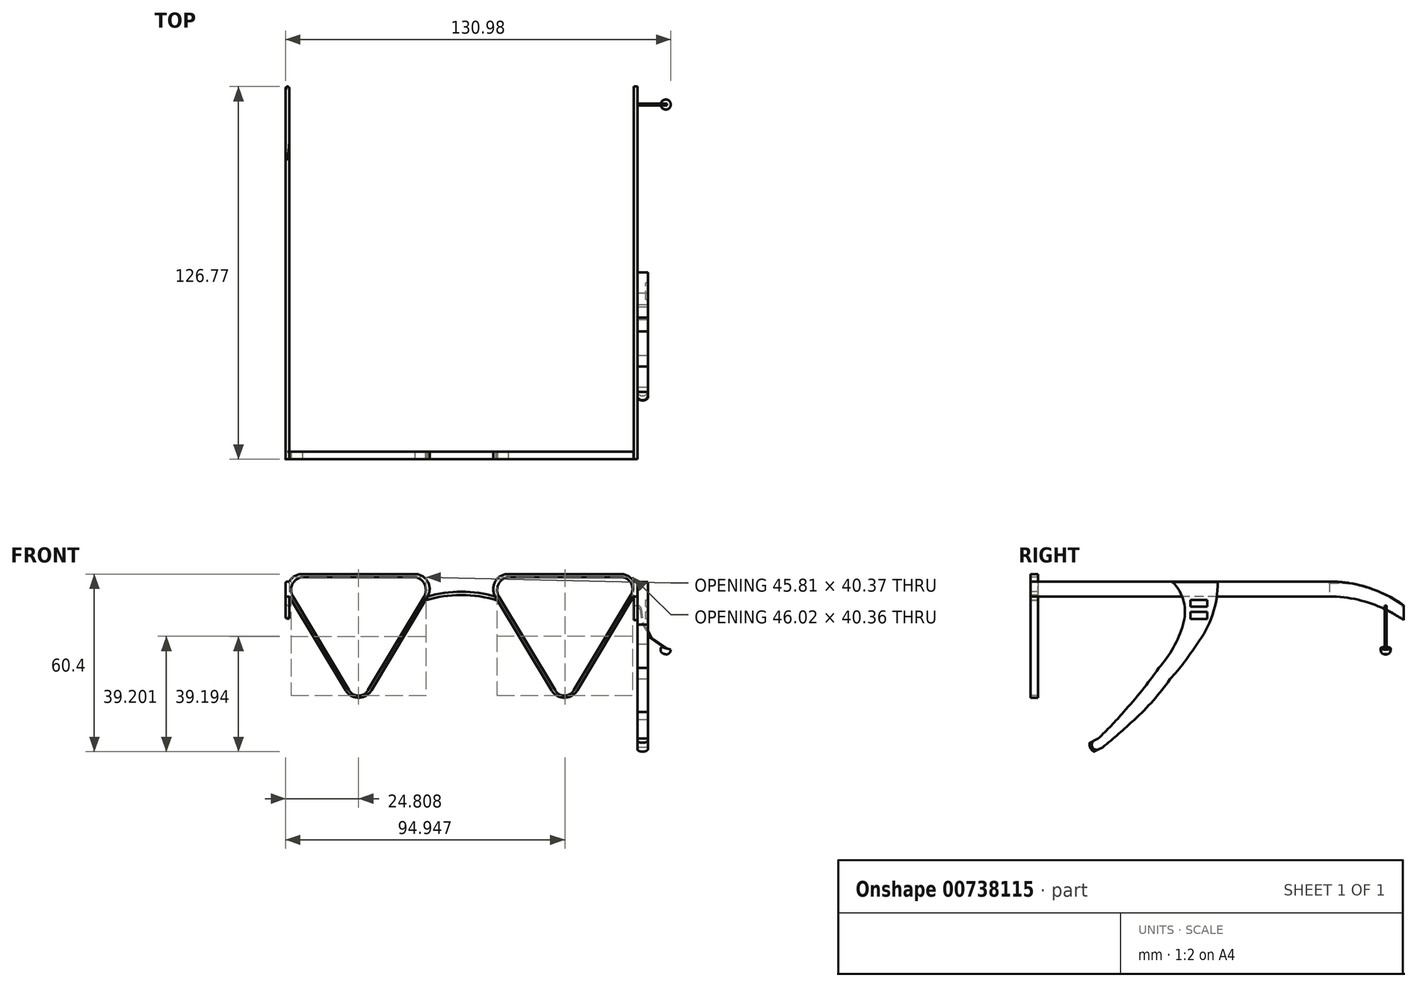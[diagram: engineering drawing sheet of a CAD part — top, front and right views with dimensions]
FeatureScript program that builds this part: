
annotation { "Feature Type Name" : "Feature", "Feature Type Description" : "" }
export const myFeature = defineFeature(function(context is Context, id is Id, definition is map)
    precondition{}
    {
        {
            var Q0;
            Q0=qCreatedBy(makeId("Front.planeOp"),FACE);
            var sketch = newSketch(context, id + "F0", { "sketchPlane" : qUnion([Q0])});
            skLineSegment(sketch, "E0", {"start": v(-99.97, 30.52) * mm, "end": v(-43.84, 30.52) * mm});
            skLineSegment(sketch, "E1", {"start": v(-71.9, -16.35) * mm, "end": v(-43.84, 30.52) * mm});
            skLineSegment(sketch, "E2", {"start": v(-99.97, 30.52) * mm, "end": v(-71.9, -16.35) * mm});
            skLineSegment(sketch, "E3.MirrorCS", {"start": v(-1.92, -16.35) * mm, "end": v(-29.99, 30.52) * mm});
            skLineSegment(sketch, "E4.MirrorCS", {"start": v(26.15, 30.52) * mm, "end": v(-29.99, 30.52) * mm});
            skLineSegment(sketch, "E5.MirrorCS", {"start": v(26.15, 30.52) * mm, "end": v(-1.92, -16.35) * mm});
            skSolve(sketch);
        }
        {
            var Q0;
            Q0=makeQuery(id+"F0.imprint","IMPRINT",FACE,{"disambiguationData":[TD([[makeQuery(id+"F0.imprint","IMPRINT",EDGE,{"derivedFrom":sQuery(id+"F0.wireOp",EDGE,"E0")}),-1.0]])]});
            var Q1;
            Q1=makeQuery(id+"F0.imprint","IMPRINT",FACE,{"disambiguationData":[TD([[makeQuery(id+"F0.imprint","IMPRINT",EDGE,{"derivedFrom":sQuery(id+"F0.wireOp",EDGE,"E3.MirrorCS")}),-1.0]])]});
            extrude(context, id + "F1", {"entities" : qUnion([Q0, Q1]), "depth" : 2.54 * mm, "offsetDistance" : 25.4 * mm});
        }
        {
            var Q0;
            Q0=makeQuery(id+"F1.opExtrude","SWEPT_EDGE",EDGE,{"disambiguationData":[OSD([sQuery(id+"F0.wireOp",EDGE,"E0"),sQuery(id+"F0.wireOp",EDGE,"E2")])]});
            var Q1;
            Q1=makeQuery(id+"F1.opExtrude","SWEPT_EDGE",EDGE,{"disambiguationData":[OSD([sQuery(id+"F0.wireOp",EDGE,"E3.MirrorCS"),sQuery(id+"F0.wireOp",EDGE,"E4.MirrorCS")])]});
            var Q2;
            Q2=makeQuery(id+"F1.opExtrude","SWEPT_EDGE",EDGE,{"disambiguationData":[OSD([sQuery(id+"F0.wireOp",EDGE,"E0"),sQuery(id+"F0.wireOp",EDGE,"E1")])]});
            var Q3;
            Q3=makeQuery(id+"F1.opExtrude","SWEPT_EDGE",EDGE,{"disambiguationData":[OSD([sQuery(id+"F0.wireOp",EDGE,"E4.MirrorCS"),sQuery(id+"F0.wireOp",EDGE,"E5.MirrorCS")])]});
            var Q4;
            Q4=makeQuery(id+"F1.opExtrude","SWEPT_EDGE",EDGE,{"disambiguationData":[OSD([sQuery(id+"F0.wireOp",EDGE,"E1"),sQuery(id+"F0.wireOp",EDGE,"E2")])]});
            var Q5;
            Q5=makeQuery(id+"F1.opExtrude","SWEPT_EDGE",EDGE,{"disambiguationData":[OSD([sQuery(id+"F0.wireOp",EDGE,"E3.MirrorCS"),sQuery(id+"F0.wireOp",EDGE,"E5.MirrorCS")])]});
            fillet(context, id + "F2", {"entities" : qUnion([Q0, Q1, Q2, Q3, Q4, Q5]), "radius" : 5.08 * mm, "tangentPropagation" : true, "allowEdgeOverflow" : false});
        }
        {
            var Q0;
            Q0=makeQuery(id+"F1.opExtrude","CAP_FACE",FACE,{"disambiguationData":[OSD([sQuery(id+"F0.wireOp",EDGE,"E0"),sQuery(id+"F0.wireOp",EDGE,"E1"),sQuery(id+"F0.wireOp",EDGE,"E2")])],"isStart":false});
            var sketch = newSketch(context, id + "F3", { "sketchPlane" : qUnion([Q0])});
            skArc(sketch, "E6", {"start": v(-25.37, 22.83) * mm, "mid": v(-36.9, 24.47) * mm, "end": v(-48.44, 22.83) * mm});
            skArc(sketch, "E7", {"start": v(-24.64, 21.5) * mm, "mid": v(-36.93, 23.39) * mm, "end": v(-49.22, 21.52) * mm});
            skLineSegment(sketch, "E8", {"start": v(-48.44, 22.83) * mm, "end": v(-49.22, 21.52) * mm});
            skLineSegment(sketch, "E9", {"start": v(-25.37, 22.83) * mm, "end": v(-24.64, 21.5) * mm});
            skSolve(sketch);
        }
        {
            var Q0;
            Q0=makeQuery(id+"F3.imprint","IMPRINT",FACE,{"disambiguationData":[TD([[makeQuery(id+"F3.imprint","IMPRINT",EDGE,{"derivedFrom":sQuery(id+"F3.wireOp",EDGE,"E6")}),1.0]])]});
            extrude(context, id + "F4", {"entities" : qUnion([Q0]), "oppositeDirection" : true, "depth" : 2.54 * mm, "offsetDistance" : 25.4 * mm});
        }
        {
            var Q0;
            Q0=makeQuery(id+"F1.opExtrude","CAP_FACE",FACE,{"disambiguationData":[OSD([sQuery(id+"F0.wireOp",EDGE,"E0"),sQuery(id+"F0.wireOp",EDGE,"E1"),sQuery(id+"F0.wireOp",EDGE,"E2")])],"isStart":false});
            var sketch = newSketch(context, id + "F5", { "sketchPlane" : qUnion([Q0])});
            skLineSegment(sketch, "E10", {"start": v(-94.18, 22.83) * mm, "end": v(-75.08, -9.07) * mm});
            skLineSegment(sketch, "E11", {"start": v(-91, 29.5) * mm, "end": v(-52.8, 29.5) * mm});
            skLineSegment(sketch, "E12", {"start": v(-49.62, 22.83) * mm, "end": v(-68.73, -9.07) * mm});
            skArc(sketch, "E13", {"start": v(-49.62, 22.83) * mm, "mid": v(-49.42, 27.01) * mm, "end": v(-52.8, 29.5) * mm});
            skArc(sketch, "E14", {"start": v(-91, 29.5) * mm, "mid": v(-94.38, 27.01) * mm, "end": v(-94.18, 22.83) * mm});
            skArc(sketch, "E15", {"start": v(-75.08, -9.07) * mm, "mid": v(-71.9, -10.87) * mm, "end": v(-68.73, -9.07) * mm});
            skSolve(sketch);
        }
        {
            var Q0;
            Q0=makeQuery(id+"F1.opExtrude","CAP_FACE",FACE,{"disambiguationData":[OSD([sQuery(id+"F0.wireOp",EDGE,"E3.MirrorCS"),sQuery(id+"F0.wireOp",EDGE,"E4.MirrorCS"),sQuery(id+"F0.wireOp",EDGE,"E5.MirrorCS")])],"isStart":false});
            var sketch = newSketch(context, id + "F6", { "sketchPlane" : qUnion([Q0])});
            skLineSegment(sketch, "E16", {"start": v(-24.15, 22.83) * mm, "end": v(-5.05, -9.07) * mm});
            skLineSegment(sketch, "E17", {"start": v(-21.02, 29.5) * mm, "end": v(17.19, 29.5) * mm});
            skLineSegment(sketch, "E18", {"start": v(20.67, 23.35) * mm, "end": v(1.26, -9.07) * mm});
            skArc(sketch, "E19", {"start": v(-21.02, 29.5) * mm, "mid": v(-24.36, 27) * mm, "end": v(-24.15, 22.83) * mm});
            skArc(sketch, "E20", {"start": v(20.67, 23.35) * mm, "mid": v(20.72, 27.44) * mm, "end": v(17.19, 29.5) * mm});
            skArc(sketch, "E21", {"start": v(-5.05, -9.07) * mm, "mid": v(-1.9, -10.86) * mm, "end": v(1.26, -9.07) * mm});
            skSolve(sketch);
        }
        {
            var Q0;
            Q0=makeQuery(id+"F5.imprint","IMPRINT",FACE,{"disambiguationData":[TD([[makeQuery(id+"F5.imprint","IMPRINT",EDGE,{"derivedFrom":sQuery(id+"F5.wireOp",EDGE,"E10")}),1.0]])]});
            var Q1;
            Q1=makeQuery(id+"F6.imprint","IMPRINT",FACE,{"disambiguationData":[TD([[makeQuery(id+"F6.imprint","IMPRINT",EDGE,{"derivedFrom":sQuery(id+"F6.wireOp",EDGE,"E16")}),1.0]])]});
            extrude(context, id + "F7", {"entities" : qUnion([Q0, Q1]), "operationType" : NewBodyOperationType.REMOVE, "oppositeDirection" : true, "depth" : 2.54 * mm, "offsetDistance" : 25.4 * mm});
        }
        {
            var Q0;
            Q0=makeQuery(id+"F1.opExtrude","CAP_FACE",FACE,{"disambiguationData":[OSD([sQuery(id+"F0.wireOp",EDGE,"E3.MirrorCS"),sQuery(id+"F0.wireOp",EDGE,"E4.MirrorCS"),sQuery(id+"F0.wireOp",EDGE,"E5.MirrorCS")])],"isStart":false});
            var sketch = newSketch(context, id + "F8", { "sketchPlane" : qUnion([Q0])});
            skLineSegment(sketch, "E22", {"start": v(21.6, 27.94) * mm, "end": v(22.88, 27.94) * mm});
            skLineSegment(sketch, "E23", {"start": v(22.88, 27.94) * mm, "end": v(22.88, 22.86) * mm});
            skLineSegment(sketch, "E24", {"start": v(22.88, 22.86) * mm, "end": v(21.6, 22.86) * mm});
            skLineSegment(sketch, "E25", {"start": v(21.6, 27.94) * mm, "end": v(21.6, 22.86) * mm});
            skSolve(sketch);
        }
        {
            var Q0;
            Q0=makeQuery(id+"F1.opExtrude","CAP_FACE",FACE,{"disambiguationData":[OSD([sQuery(id+"F0.wireOp",EDGE,"E0"),sQuery(id+"F0.wireOp",EDGE,"E1"),sQuery(id+"F0.wireOp",EDGE,"E2")])],"isStart":false});
            var sketch = newSketch(context, id + "F9", { "sketchPlane" : qUnion([Q0])});
            skLineSegment(sketch, "E26", {"start": v(-95.43, 27.94) * mm, "end": v(-96.7, 27.94) * mm});
            skLineSegment(sketch, "E27", {"start": v(-96.7, 27.94) * mm, "end": v(-96.7, 22.86) * mm});
            skLineSegment(sketch, "E28", {"start": v(-96.7, 22.86) * mm, "end": v(-95.44, 22.86) * mm});
            skLineSegment(sketch, "E29", {"start": v(-95.43, 27.94) * mm, "end": v(-95.44, 22.86) * mm});
            skSolve(sketch);
        }
        {
            var Q0;
            {var subQ0=sQuery(id+"F9.wireOp",EDGE,"E26");Q0=makeQuery(id+"F9.imprint","IMPRINT",FACE,{"disambiguationData":[TD([[makeQuery(id+"F9.imprint","IMPRINT",EDGE,{"derivedFrom":subQ0}),1.0]])]});}
            var Q1;
            {var subQ0=sQuery(id+"F8.wireOp",EDGE,"E22");Q1=makeQuery(id+"F8.imprint","IMPRINT",FACE,{"disambiguationData":[TD([[makeQuery(id+"F8.imprint","IMPRINT",EDGE,{"derivedFrom":subQ0}),-1.0]])]});}
            var Q2;
            {var subQ0=sQuery(id+"F9.wireOp",EDGE,"E29");var subQ1=sQuery(id+"F0.wireOp",EDGE,"E2");var subQ2=sQuery(id+"F0.wireOp",EDGE,"E0");var subQ3=makeQuery(id+"F2.opFillet","BLEND_EDGE",EDGE,{"blendedFrom":[makeQuery(id+"F1.opExtrude","SWEPT_EDGE",EDGE,{"disambiguationData":[OSD([subQ2,subQ1])]}),makeQuery(id+"F1.opExtrude","CAP_FACE",FACE,{"disambiguationData":[OSD([subQ2,sQuery(id+"F0.wireOp",EDGE,"E1"),subQ1])],"isStart":false})],"blendedInto":[makeQuery(id+"F1.opExtrude","CAP_FACE",FACE,{"disambiguationData":[OSD([subQ2,sQuery(id+"F0.wireOp",EDGE,"E1"),subQ1])],"isStart":false})]});var subQ5=makeQuery(id+"F9.imprint","INTERSECT",VERTEX,{"derivedFrom":[subQ3,subQ0]});Q2=makeQuery(id+"F9.imprint","IMPRINT",FACE,{"disambiguationData":[TD([[makeQuery(id+"F9.imprint","IMPRINT",EDGE,{"disambiguationData":[TD([[subQ5,1.0]])],"derivedFrom":subQ0}),-1.0]])]});}
            var Q3;
            {var subQ0=sQuery(id+"F8.wireOp",EDGE,"E25");var subQ1=sQuery(id+"F0.wireOp",EDGE,"E5.MirrorCS");var subQ2=sQuery(id+"F0.wireOp",EDGE,"E4.MirrorCS");var subQ3=makeQuery(id+"F2.opFillet","BLEND_EDGE",EDGE,{"blendedFrom":[makeQuery(id+"F1.opExtrude","SWEPT_EDGE",EDGE,{"disambiguationData":[OSD([subQ2,subQ1])]}),makeQuery(id+"F1.opExtrude","CAP_FACE",FACE,{"disambiguationData":[OSD([sQuery(id+"F0.wireOp",EDGE,"E3.MirrorCS"),subQ2,subQ1])],"isStart":false})],"blendedInto":[makeQuery(id+"F1.opExtrude","CAP_FACE",FACE,{"disambiguationData":[OSD([sQuery(id+"F0.wireOp",EDGE,"E3.MirrorCS"),subQ2,subQ1])],"isStart":false})]});var subQ5=makeQuery(id+"F8.imprint","INTERSECT",VERTEX,{"derivedFrom":[subQ3,subQ0]});Q3=makeQuery(id+"F8.imprint","IMPRINT",FACE,{"disambiguationData":[TD([[makeQuery(id+"F8.imprint","IMPRINT",EDGE,{"disambiguationData":[TD([[subQ5,1.0]])],"derivedFrom":subQ0}),1.0]])]});}
            extrude(context, id + "F10", {"entities" : qUnion([Q0, Q1, Q2, Q3]), "operationType" : NewBodyOperationType.ADD, "oppositeDirection" : true, "depth" : 101.6 * mm, "offsetDistance" : 25.4 * mm});
        }
        {
            var Q0;
            Q0=makeQuery(id+"F10.opExtrude","SWEPT_FACE",FACE,{"disambiguationData":[OSD([sQuery(id+"F9.wireOp",EDGE,"E27")])]});
            var sketch = newSketch(context, id + "F11", { "sketchPlane" : qUnion([Q0])});
            skArc(sketch, "E30", {"start": v(-99.06, 27.94) * mm, "mid": v(-112.27, 25.87) * mm, "end": v(-124.21, 19.86) * mm});
            skLineSegment(sketch, "E31", {"start": v(-124.21, 19.86) * mm, "end": v(-124.21, 14.78) * mm});
            skArc(sketch, "E32", {"start": v(-99.06, 22.86) * mm, "mid": v(-112.27, 20.8) * mm, "end": v(-124.21, 14.78) * mm});
            skSolve(sketch);
        }
        {
            var Q0;
            Q0=makeQuery(id+"F10.opExtrude","SWEPT_FACE",FACE,{"disambiguationData":[OSD([sQuery(id+"F8.wireOp",EDGE,"E23")])]});
            var sketch = newSketch(context, id + "F12", { "sketchPlane" : qUnion([Q0])});
            skArc(sketch, "E33", {"start": v(124.23, 19.82) * mm, "mid": v(112.28, 25.86) * mm, "end": v(99.06, 27.94) * mm});
            skArc(sketch, "E34", {"start": v(124.23, 14.83) * mm, "mid": v(112.27, 20.8) * mm, "end": v(99.06, 22.86) * mm});
            skLineSegment(sketch, "E35", {"start": v(124.23, 19.82) * mm, "end": v(124.23, 14.83) * mm});
            skSolve(sketch);
        }
        {
            var Q0;
            Q0=makeQuery(id+"F12.imprint","IMPRINT",FACE,{"disambiguationData":[TD([[makeQuery(id+"F12.imprint","IMPRINT",EDGE,{"derivedFrom":sQuery(id+"F12.wireOp",EDGE,"E33")}),1.0]])]});
            extrude(context, id + "F13", {"entities" : qUnion([Q0]), "operationType" : NewBodyOperationType.ADD, "oppositeDirection" : true, "depth" : 1.27 * mm, "offsetDistance" : 25.4 * mm});
        }
        {
            var Q0;
            Q0=makeQuery(id+"F11.imprint","IMPRINT",FACE,{"disambiguationData":[TD([[makeQuery(id+"F11.imprint","IMPRINT",EDGE,{"derivedFrom":sQuery(id+"F11.wireOp",EDGE,"E30")}),1.0]])]});
            extrude(context, id + "F14", {"entities" : qUnion([Q0]), "operationType" : NewBodyOperationType.ADD, "oppositeDirection" : true, "depth" : 1.27 * mm, "offsetDistance" : 25.4 * mm});
        }
        {
            var Q0;
            Q0=makeQuery(id+"F10.opExtrude","SWEPT_EDGE",EDGE,{"disambiguationData":[OSD([sQuery(id+"F9.wireOp",EDGE,"E26"),sQuery(id+"F9.wireOp",EDGE,"E27")])]});
            var Q1;
            Q1=makeQuery(id+"F10.opExtrude","SWEPT_EDGE",EDGE,{"disambiguationData":[OSD([sQuery(id+"F9.wireOp",EDGE,"E27"),sQuery(id+"F9.wireOp",EDGE,"E28")])]});
            var Q2;
            {var subQ0=sQuery(id+"F9.wireOp",EDGE,"E26");var subQ1=sQuery(id+"F9.wireOp",EDGE,"E29");Q2=makeQuery(id+"F10.boolean.opBoolean","SPLIT",EDGE,{"disambiguationData":[topologyDisambiguationEdgeConnected([makeQuery(id+"F10.opExtrude","SWEPT_FACE",FACE,{"disambiguationData":[OSD([subQ1])]})])],"derivedFrom":makeQuery(id+"F10.opExtrude","SWEPT_EDGE",EDGE,{"disambiguationData":[OSD([sQuery(id+"F0.wireOp",EDGE,"E0"),sQuery(id+"F0.wireOp",EDGE,"E1"),sQuery(id+"F0.wireOp",EDGE,"E2"),subQ0,subQ1])]})});}
            fillet(context, id + "F15", {"entities" : qUnion([Q0, Q1, Q2]), "radius" : 0.64 * mm, "tangentPropagation" : true, "allowEdgeOverflow" : false});
        }
        {
            var Q0;
            Q0=makeQuery(id+"F14.opExtrude","CAP_EDGE",EDGE,{"disambiguationData":[OSD([sQuery(id+"F11.wireOp",EDGE,"E31")])],"isStart":false});
            var Q1;
            Q1=makeQuery(id+"F14.opExtrude","CAP_EDGE",EDGE,{"disambiguationData":[OSD([sQuery(id+"F11.wireOp",EDGE,"E31")])],"isStart":true});
            fillet(context, id + "F16", {"entities" : qUnion([Q0, Q1]), "radius" : 0.64 * mm, "tangentPropagation" : true, "allowEdgeOverflow" : false});
        }
        {
            var Q0;
            Q0=makeQuery(id+"F13.opExtrude","SWEPT_FACE",FACE,{"disambiguationData":[OSD([sQuery(id+"F12.wireOp",EDGE,"E35")])]});
            var sketch = newSketch(context, id + "F17", { "sketchPlane" : qUnion([Q0])});
            skArc(sketch, "E36", {"start": v(-22.88, 19.82) * mm, "mid": v(-23.8, 19.47) * mm, "end": v(-24.26, 18.6) * mm});
            skArc(sketch, "E37", {"start": v(-22.88, 19.31) * mm, "mid": v(-23.45, 18.99) * mm, "end": v(-23.81, 18.44) * mm});
            skLineSegment(sketch, "E38", {"start": v(-22.88, 19.82) * mm, "end": v(-22.88, 19.31) * mm});
            skLineSegment(sketch, "E39", {"start": v(-24.26, 18.6) * mm, "end": v(-24.88, 13.74) * mm});
            skLineSegment(sketch, "E40", {"start": v(-23.81, 18.44) * mm, "end": v(-24.42, 13.74) * mm});
            skLineSegment(sketch, "E41", {"start": v(-24.42, 13.74) * mm, "end": v(-27.35, 8.77) * mm});
            skLineSegment(sketch, "E42", {"start": v(-24.88, 13.74) * mm, "end": v(-27.82, 8.77) * mm});
            skLineSegment(sketch, "E43", {"start": v(-27.82, 8.77) * mm, "end": v(-33, 5.17) * mm});
            skLineSegment(sketch, "E44", {"start": v(-27.35, 8.77) * mm, "end": v(-32.25, 5.36) * mm});
            skLineSegment(sketch, "E45", {"start": v(-33, 5.17) * mm, "end": v(-32.25, 5.36) * mm});
            skSolve(sketch);
        }
        {
            var Q0;
            Q0=makeQuery(id+"F17.imprint","IMPRINT",FACE,{"disambiguationData":[TD([[makeQuery(id+"F17.imprint","IMPRINT",EDGE,{"derivedFrom":sQuery(id+"F17.wireOp",EDGE,"E36")}),1.0]])]});
            extrude(context, id + "F18", {"entities" : qUnion([Q0]), "operationType" : NewBodyOperationType.ADD, "oppositeDirection" : true, "depth" : 6.43 * mm, "offsetDistance" : 25.4 * mm, "hasSecondDirection" : true, "secondDirectionOppositeDirection" : true, "secondDirectionDepth" : 5.82 * mm});
        }
        {
            var Q0;
            Q0=makeQuery(id+"F18.opExtrude","SWEPT_FACE",FACE,{"disambiguationData":[OSD([sQuery(id+"F17.wireOp",EDGE,"E45")])]});
            var sketch = newSketch(context, id + "F19", { "sketchPlane" : qUnion([Q0])});
            skCircle(sketch, "E46", {"center": v(30.22, -118.1) * mm, "radius": 1.7 * mm});
            skPoint(sketch, "E46.centerSnap0", {"position": v(30.22, -117.8) * mm});
            skPoint(sketch, "E46.centerSnap1", {"position": v(30.6, -118.1) * mm});
            skSolve(sketch);
        }
        {
            var Q0;
            Q0=makeQuery(id+"F19.imprint","IMPRINT",FACE,{"disambiguationData":[TD([[makeQuery(id+"F19.imprint","IMPRINT",EDGE,{"derivedFrom":sQuery(id+"F19.wireOp",EDGE,"E46")}),1.0]])]});
            var Q1;
            {var subQ0=sQuery(id+"F17.wireOp",EDGE,"E45");Q1=makeQuery(id+"F19.imprint","IMPRINT",FACE,{"disambiguationData":[TD([[makeQuery(id+"F19.imprint","IMPRINT",EDGE,{"derivedFrom":makeQuery(id+"F18.opExtrude","CAP_EDGE",EDGE,{"disambiguationData":[OSD([subQ0])],"isStart":true})}),-1.0]])]});}
            extrude(context, id + "F20", {"entities" : qUnion([Q0, Q1]), "operationType" : NewBodyOperationType.ADD, "depth" : 2.03 * mm, "offsetDistance" : 25.4 * mm});
        }
        {
            var Q0;
            Q0=makeQuery(id+"F20.opExtrude","CAP_EDGE",EDGE,{"disambiguationData":[OSD([sQuery(id+"F19.wireOp",EDGE,"E46")])],"isStart":false});
            fillet(context, id + "F21", {"entities" : qUnion([Q0]), "radius" : 1.4 * mm, "tangentPropagation" : true, "allowEdgeOverflow" : false});
        }
        {
            var Q0;
            Q0=makeQuery(id+"F20.opExtrude","CAP_FACE",FACE,{"disambiguationData":[OSD([sQuery(id+"F19.wireOp",EDGE,"E46")])],"isStart":false});
            var sketch = newSketch(context, id + "F22", { "sketchPlane" : qUnion([Q0])});
            skCircle(sketch, "E47", {"center": v(30.47, -118.15) * mm, "radius": 0.02 * mm});
            skCircle(sketch, "E48", {"center": v(30.45, -118.2) * mm, "radius": 0.02 * mm});
            skCircle(sketch, "E49", {"center": v(30.41, -118.24) * mm, "radius": 0.02 * mm});
            skCircle(sketch, "E50", {"center": v(30.37, -118.3) * mm, "radius": 0.02 * mm});
            skCircle(sketch, "E51", {"center": v(30.33, -118.35) * mm, "radius": 0.02 * mm});
            skCircle(sketch, "E52", {"center": v(30.43, -118.3) * mm, "radius": 0.02 * mm});
            skCircle(sketch, "E53", {"center": v(30.4, -118.15) * mm, "radius": 0.02 * mm});
            skCircle(sketch, "E54", {"center": v(30.38, -118.2) * mm, "radius": 0.01 * mm});
            skCircle(sketch, "E55", {"center": v(30.35, -118.24) * mm, "radius": 0.02 * mm});
            skCircle(sketch, "E56", {"center": v(30.3, -118.3) * mm, "radius": 0.02 * mm});
            skCircle(sketch, "E57", {"center": v(30.26, -118.34) * mm, "radius": 0.03 * mm});
            skCircle(sketch, "E58", {"center": v(30.25, -118.3) * mm, "radius": 0.02 * mm});
            skCircle(sketch, "E59", {"center": v(30.29, -118.2) * mm, "radius": 0.02 * mm});
            skCircle(sketch, "E60", {"center": v(30.33, -118.15) * mm, "radius": 0.02 * mm});
            skCircle(sketch, "E61", {"center": v(30.28, -118.15) * mm, "radius": 0.02 * mm});
            skCircle(sketch, "E62", {"center": v(30.24, -118.2) * mm, "radius": 0.01 * mm});
            skCircle(sketch, "E63", {"center": v(30.24, -118.24) * mm, "radius": 0.02 * mm});
            skCircle(sketch, "E64.MirrorC", {"center": v(29.96, -118.15) * mm, "radius": 0.02 * mm});
            skCircle(sketch, "E65.MirrorC", {"center": v(29.99, -118.2) * mm, "radius": 0.02 * mm});
            skCircle(sketch, "E66.MirrorC", {"center": v(30.02, -118.24) * mm, "radius": 0.02 * mm});
            skCircle(sketch, "E67.MirrorC", {"center": v(30, -118.3) * mm, "radius": 0.02 * mm});
            skCircle(sketch, "E68.MirrorC", {"center": v(30.06, -118.3) * mm, "radius": 0.02 * mm});
            skCircle(sketch, "E69.MirrorC", {"center": v(30.08, -118.24) * mm, "radius": 0.02 * mm});
            skCircle(sketch, "E70.MirrorC", {"center": v(30.05, -118.2) * mm, "radius": 0.01 * mm});
            skCircle(sketch, "E71.MirrorC", {"center": v(30.04, -118.15) * mm, "radius": 0.02 * mm});
            skCircle(sketch, "E72.MirrorC", {"center": v(30.1, -118.15) * mm, "radius": 0.02 * mm});
            skCircle(sketch, "E73.MirrorC", {"center": v(30.16, -118.15) * mm, "radius": 0.02 * mm});
            skCircle(sketch, "E74.MirrorC", {"center": v(30.15, -118.2) * mm, "radius": 0.02 * mm});
            skCircle(sketch, "E75.MirrorC", {"center": v(30.2, -118.2) * mm, "radius": 0.01 * mm});
            skCircle(sketch, "E76.MirrorC", {"center": v(30.2, -118.24) * mm, "radius": 0.02 * mm});
            skCircle(sketch, "E77.MirrorC", {"center": v(30.18, -118.3) * mm, "radius": 0.02 * mm});
            skCircle(sketch, "E78.MirrorC", {"center": v(30.17, -118.34) * mm, "radius": 0.03 * mm});
            skCircle(sketch, "E79.MirrorC", {"center": v(30.14, -118.3) * mm, "radius": 0.02 * mm});
            skCircle(sketch, "E80.MirrorC", {"center": v(30.1, -118.35) * mm, "radius": 0.02 * mm});
            skCircle(sketch, "E81.MirrorC", {"center": v(30.47, -118.06) * mm, "radius": 0.02 * mm});
            skCircle(sketch, "E82.MirrorC", {"center": v(30.45, -118.02) * mm, "radius": 0.02 * mm});
            skCircle(sketch, "E83.MirrorC", {"center": v(30.4, -118.06) * mm, "radius": 0.02 * mm});
            skCircle(sketch, "E84.MirrorC", {"center": v(30.33, -118.06) * mm, "radius": 0.02 * mm});
            skCircle(sketch, "E85.MirrorC", {"center": v(30.28, -118.06) * mm, "radius": 0.02 * mm});
            skCircle(sketch, "E86.MirrorC", {"center": v(30.16, -118.06) * mm, "radius": 0.02 * mm});
            skCircle(sketch, "E87.MirrorC", {"center": v(30.1, -118.06) * mm, "radius": 0.02 * mm});
            skCircle(sketch, "E88.MirrorC", {"center": v(30.04, -118.06) * mm, "radius": 0.02 * mm});
            skCircle(sketch, "E89.MirrorC", {"center": v(29.96, -118.06) * mm, "radius": 0.02 * mm});
            skCircle(sketch, "E90.MirrorC", {"center": v(29.99, -118.02) * mm, "radius": 0.02 * mm});
            skCircle(sketch, "E91.MirrorC", {"center": v(30.05, -118.01) * mm, "radius": 0.01 * mm});
            skCircle(sketch, "E92.MirrorC", {"center": v(30.02, -117.97) * mm, "radius": 0.02 * mm});
            skCircle(sketch, "E93.MirrorC", {"center": v(30, -117.92) * mm, "radius": 0.02 * mm});
            skCircle(sketch, "E94.MirrorC", {"center": v(30.06, -117.92) * mm, "radius": 0.02 * mm});
            skCircle(sketch, "E95.MirrorC", {"center": v(30.08, -117.97) * mm, "radius": 0.02 * mm});
            skCircle(sketch, "E96.MirrorC", {"center": v(30.1, -117.86) * mm, "radius": 0.02 * mm});
            skCircle(sketch, "E97.MirrorC", {"center": v(30.17, -117.87) * mm, "radius": 0.03 * mm});
            skCircle(sketch, "E98.MirrorC", {"center": v(30.18, -117.92) * mm, "radius": 0.02 * mm});
            skCircle(sketch, "E99.MirrorC", {"center": v(30.14, -117.92) * mm, "radius": 0.02 * mm});
            skCircle(sketch, "E100.MirrorC", {"center": v(30.2, -117.97) * mm, "radius": 0.02 * mm});
            skCircle(sketch, "E101.MirrorC", {"center": v(30.2, -118.02) * mm, "radius": 0.01 * mm});
            skCircle(sketch, "E102.MirrorC", {"center": v(30.15, -118.01) * mm, "radius": 0.02 * mm});
            skCircle(sketch, "E103.MirrorC", {"center": v(30.24, -118.02) * mm, "radius": 0.01 * mm});
            skCircle(sketch, "E104.MirrorC", {"center": v(30.24, -117.97) * mm, "radius": 0.02 * mm});
            skCircle(sketch, "E105.MirrorC", {"center": v(30.25, -117.92) * mm, "radius": 0.02 * mm});
            skCircle(sketch, "E106.MirrorC", {"center": v(30.26, -117.87) * mm, "radius": 0.03 * mm});
            skCircle(sketch, "E107.MirrorC", {"center": v(30.33, -117.86) * mm, "radius": 0.02 * mm});
            skCircle(sketch, "E108.MirrorC", {"center": v(30.3, -117.92) * mm, "radius": 0.02 * mm});
            skCircle(sketch, "E109.MirrorC", {"center": v(30.35, -117.97) * mm, "radius": 0.02 * mm});
            skCircle(sketch, "E110.MirrorC", {"center": v(30.37, -117.92) * mm, "radius": 0.02 * mm});
            skCircle(sketch, "E111.MirrorC", {"center": v(30.43, -117.92) * mm, "radius": 0.02 * mm});
            skCircle(sketch, "E112.MirrorC", {"center": v(30.41, -117.97) * mm, "radius": 0.02 * mm});
            skCircle(sketch, "E113.MirrorC", {"center": v(30.38, -118.01) * mm, "radius": 0.01 * mm});
            skCircle(sketch, "E114.MirrorC", {"center": v(30.29, -118.01) * mm, "radius": 0.02 * mm});
            skSolve(sketch);
        }
        {
            var Q0;
            Q0 = qSketchRegion(id + "F22", true);
            extrude(context, id + "F23", {"entities" : qUnion([Q0]), "operationType" : NewBodyOperationType.REMOVE, "oppositeDirection" : true, "depth" : 0.25 * mm, "offsetDistance" : 25.4 * mm});
        }
        {
            var Q0;
            Q0 = qSketchRegion(id + "F5", true);
            var Q1;
            Q1 = qSketchRegion(id + "F6", true);
            extrude(context, id + "F24", {"entities" : qUnion([Q0, Q1]), "oppositeDirection" : true, "depth" : 2.54 * mm, "offsetDistance" : 25.4 * mm});
        }
        {
            var Q0;
            {var subQ0=sQuery(id+"F8.wireOp",EDGE,"E23");Q0=makeQuery(id+"F13.boolean.opBoolean","MERGE",FACE,{"derivedFrom":[makeQuery(id+"F10.opExtrude","SWEPT_FACE",FACE,{"disambiguationData":[OSD([subQ0])]}),makeQuery(id+"F13.opExtrude","CAP_FACE",FACE,{"disambiguationData":[OSD([subQ0,sQuery(id+"F12.wireOp",EDGE,"E33"),sQuery(id+"F12.wireOp",EDGE,"E34"),sQuery(id+"F12.wireOp",EDGE,"E35")])],"isStart":true})]});}
            var sketch = newSketch(context, id + "F25", { "sketchPlane" : qUnion([Q0])});
            skPoint(sketch, "E115", {"position": v(45.6, 27.82) * mm});
            skPoint(sketch, "E116", {"position": v(61.07, 27.82) * mm});
            skPoint(sketch, "E117", {"position": v(53.87, 6.63) * mm});
            skPoint(sketch, "E118", {"position": v(49.23, 13.35) * mm});
            skPoint(sketch, "E119", {"position": v(41.02, -1.42) * mm});
            skPoint(sketch, "E120", {"position": v(44.84, -5.24) * mm});
            skArc(sketch, "E121", {"start": v(53.87, 6.63) * mm, "mid": v(59.28, 16.62) * mm, "end": v(61.07, 27.82) * mm});
            skArc(sketch, "E122", {"start": v(49.23, 13.35) * mm, "mid": v(49.51, 21.11) * mm, "end": v(45.6, 27.82) * mm});
            skArc(sketch, "E123", {"start": v(44.84, -5.24) * mm, "mid": v(49.63, 0.49) * mm, "end": v(53.87, 6.63) * mm});
            skArc(sketch, "E124", {"start": v(41.02, -1.42) * mm, "mid": v(45.96, 5.5) * mm, "end": v(49.23, 13.35) * mm});
            skLineSegment(sketch, "E125", {"start": v(45.6, 27.82) * mm, "end": v(61.07, 27.82) * mm});
            skPoint(sketch, "E126", {"position": v(32.7, -19.03) * mm});
            skPoint(sketch, "E127", {"position": v(29, -16.43) * mm});
            skArc(sketch, "E128", {"start": v(32.7, -19.03) * mm, "mid": v(39.14, -12.47) * mm, "end": v(44.84, -5.24) * mm});
            skArc(sketch, "E129", {"start": v(29, -16.43) * mm, "mid": v(35.26, -9.13) * mm, "end": v(41.02, -1.42) * mm});
            skArc(sketch, "E130", {"start": v(20.41, -25.44) * mm, "mid": v(24.82, -21.05) * mm, "end": v(29, -16.43) * mm});
            skArc(sketch, "E131", {"start": v(21.91, -28.44) * mm, "mid": v(27.38, -23.83) * mm, "end": v(32.7, -19.03) * mm});
            skLineSegment(sketch, "E132", {"start": v(20.41, -25.44) * mm, "end": v(21.91, -28.44) * mm});
            skSolve(sketch);
        }
        {
            var Q0;
            {var subQ0=sQuery(id+"F25.wireOp",EDGE,"E123");Q0=makeQuery(id+"F25.imprint","IMPRINT",FACE,{"disambiguationData":[TD([[makeQuery(id+"F25.imprint","IMPRINT",EDGE,{"derivedFrom":subQ0}),1.0]])]});}
            var Q1;
            {var subQ0=sQuery(id+"F25.wireOp",EDGE,"E132");Q1=makeQuery(id+"F25.imprint","IMPRINT",FACE,{"disambiguationData":[TD([[makeQuery(id+"F25.imprint","IMPRINT",EDGE,{"derivedFrom":subQ0}),1.0]])]});}
            var Q2;
            {var subQ0=sQuery(id+"F25.wireOp",EDGE,"E125");Q2=makeQuery(id+"F25.imprint","IMPRINT",FACE,{"disambiguationData":[TD([[makeQuery(id+"F25.imprint","IMPRINT",EDGE,{"derivedFrom":subQ0}),-1.0]])]});}
            extrude(context, id + "F26", {"entities" : qUnion([Q0, Q1, Q2]), "operationType" : NewBodyOperationType.ADD, "depth" : 3.56 * mm, "offsetDistance" : 25.4 * mm});
        }
        {
            var Q0;
            Q0=makeQuery(id+"F26.opExtrude","SWEPT_FACE",FACE,{"disambiguationData":[OSD([sQuery(id+"F25.wireOp",EDGE,"E132")])]});
            var sketch = newSketch(context, id + "F27", { "sketchPlane" : qUnion([Q0])});
            skCircle(sketch, "E133", {"center": v(24.65, -33.56) * mm, "radius": 2.44 * mm});
            skPoint(sketch, "E133.centerSnap0", {"position": v(26.43, -33.56) * mm});
            skPoint(sketch, "E133.centerSnap1", {"position": v(24.65, -31.88) * mm});
            skSolve(sketch);
        }
        {
            var Q0;
            {var subQ0=sQuery(id+"F25.wireOp",EDGE,"E132");Q0=makeQuery(id+"F27.imprint","IMPRINT",FACE,{"disambiguationData":[TD([[makeQuery(id+"F27.imprint","IMPRINT",EDGE,{"derivedFrom":makeQuery(id+"F26.opExtrude","CAP_EDGE",EDGE,{"disambiguationData":[OSD([subQ0])],"isStart":true})}),1.0]])]});}
            var Q1;
            {var subQ1=sQuery(id+"F25.wireOp",EDGE,"E132");var subQ2=makeQuery(id+"F26.opExtrude","CAP_EDGE",EDGE,{"disambiguationData":[OSD([subQ1])],"isStart":false});Q1=makeQuery(id+"F27.imprint","IMPRINT",FACE,{"disambiguationData":[TD([[makeQuery(id+"F27.imprint","IMPRINT",EDGE,{"derivedFrom":subQ2}),1.0]])]});}
            var Q2;
            {var subQ1=sQuery(id+"F25.wireOp",EDGE,"E132");var subQ2=makeQuery(id+"F26.opExtrude","SWEPT_EDGE",EDGE,{"disambiguationData":[OSD([sQuery(id+"F25.wireOp",EDGE,"E131"),subQ1])]});Q2=makeQuery(id+"F27.imprint","IMPRINT",FACE,{"disambiguationData":[TD([[makeQuery(id+"F27.imprint","IMPRINT",EDGE,{"derivedFrom":subQ2}),1.0]])]});}
            var Q3;
            {var subQ1=sQuery(id+"F25.wireOp",EDGE,"E132");var subQ2=makeQuery(id+"F26.opExtrude","CAP_EDGE",EDGE,{"disambiguationData":[OSD([subQ1])],"isStart":true});Q3=makeQuery(id+"F27.imprint","IMPRINT",FACE,{"disambiguationData":[TD([[makeQuery(id+"F27.imprint","IMPRINT",EDGE,{"derivedFrom":subQ2}),-1.0]])]});}
            var Q4;
            {var subQ1=sQuery(id+"F25.wireOp",EDGE,"E132");var subQ2=makeQuery(id+"F26.opExtrude","SWEPT_EDGE",EDGE,{"disambiguationData":[OSD([sQuery(id+"F25.wireOp",EDGE,"E130"),subQ1])]});Q4=makeQuery(id+"F27.imprint","IMPRINT",FACE,{"disambiguationData":[TD([[makeQuery(id+"F27.imprint","IMPRINT",EDGE,{"derivedFrom":subQ2}),-1.0]])]});}
            extrude(context, id + "F28", {"entities" : qUnion([Q0, Q1, Q2, Q3, Q4]), "operationType" : NewBodyOperationType.ADD, "depth" : 3.8 * mm, "offsetDistance" : 25.4 * mm});
        }
        {
            var Q0;
            Q0=makeQuery(id+"F28.opExtrude","CAP_EDGE",EDGE,{"disambiguationData":[OSD([sQuery(id+"F27.wireOp",EDGE,"E133")])],"isStart":false});
            fillet(context, id + "F29", {"entities" : qUnion([Q0]), "radius" : 2.33 * mm, "tangentPropagation" : true, "allowEdgeOverflow" : false});
        }
        {
            var Q0;
            {var subQ0=sQuery(id+"F25.wireOp",EDGE,"E131");var subQ1=sQuery(id+"F27.wireOp",EDGE,"E133");var subQ2=sQuery(id+"F25.wireOp",EDGE,"E130");var subQ3=makeQuery(id+"F28.opExtrude","CAP_FACE",FACE,{"disambiguationData":[OSD([subQ1])],"isStart":true});Q0=makeQuery(id+"F28.boolean.opBoolean","SPLIT",FACE,{"disambiguationData":[TD([makeQuery(id+"F26.opExtrude","CAP_FACE",FACE,{"disambiguationData":[OSD([sQuery(id+"F25.wireOp",EDGE,"E121"),sQuery(id+"F25.wireOp",EDGE,"E122"),sQuery(id+"F25.wireOp",EDGE,"E123"),sQuery(id+"F25.wireOp",EDGE,"E124"),sQuery(id+"F25.wireOp",EDGE,"E125"),sQuery(id+"F25.wireOp",EDGE,"E128"),sQuery(id+"F25.wireOp",EDGE,"E129"),subQ2,subQ0,sQuery(id+"F25.wireOp",EDGE,"E132")])],"isStart":false}),makeQuery(id+"F26.opExtrude","SWEPT_FACE",FACE,{"disambiguationData":[OSD([subQ2])]}),makeQuery(id+"F26.opExtrude","SWEPT_FACE",FACE,{"disambiguationData":[OSD([subQ0])]}),makeQuery(id+"F28.opExtrude","SWEPT_FACE",FACE,{"disambiguationData":[OSD([subQ1])]}),subQ3])],"derivedFrom":subQ3});}
            var Q1;
            {var subQ0=sQuery(id+"F27.wireOp",EDGE,"E133");var subQ1=sQuery(id+"F25.wireOp",EDGE,"E131");var subQ2=sQuery(id+"F25.wireOp",EDGE,"E132");var subQ3=sQuery(id+"F25.wireOp",EDGE,"E130");var subQ4=sQuery(id+"F25.wireOp",EDGE,"E129");var subQ5=sQuery(id+"F25.wireOp",EDGE,"E128");var subQ6=sQuery(id+"F25.wireOp",EDGE,"E125");var subQ7=sQuery(id+"F25.wireOp",EDGE,"E124");var subQ8=sQuery(id+"F25.wireOp",EDGE,"E123");var subQ9=sQuery(id+"F25.wireOp",EDGE,"E122");var subQ10=sQuery(id+"F25.wireOp",EDGE,"E121");var subQ11=makeQuery(id+"F28.opExtrude","CAP_FACE",FACE,{"disambiguationData":[OSD([subQ0])],"isStart":true});Q1=makeQuery(id+"F28.boolean.opBoolean","SPLIT",FACE,{"disambiguationData":[TD([makeQuery(id+"F26.opExtrude","CAP_FACE",FACE,{"disambiguationData":[OSD([subQ10,subQ9,subQ8,subQ7,subQ6,subQ5,subQ4,subQ3,subQ1,subQ2])],"isStart":true}),makeQuery(id+"F26.opExtrude","CAP_FACE",FACE,{"disambiguationData":[OSD([subQ10,subQ9,subQ8,subQ7,subQ6,subQ5,subQ4,subQ3,subQ1,subQ2])],"isStart":false}),makeQuery(id+"F26.opExtrude","SWEPT_FACE",FACE,{"disambiguationData":[OSD([subQ1])]}),makeQuery(id+"F28.opExtrude","SWEPT_FACE",FACE,{"disambiguationData":[OSD([subQ0])]}),subQ11])],"derivedFrom":subQ11});}
            var Q2;
            {var subQ0=sQuery(id+"F25.wireOp",EDGE,"E131");var subQ1=sQuery(id+"F27.wireOp",EDGE,"E133");var subQ2=sQuery(id+"F25.wireOp",EDGE,"E130");var subQ3=makeQuery(id+"F28.opExtrude","CAP_FACE",FACE,{"disambiguationData":[OSD([subQ1])],"isStart":true});Q2=makeQuery(id+"F28.boolean.opBoolean","SPLIT",FACE,{"disambiguationData":[TD([makeQuery(id+"F26.opExtrude","CAP_FACE",FACE,{"disambiguationData":[OSD([sQuery(id+"F25.wireOp",EDGE,"E121"),sQuery(id+"F25.wireOp",EDGE,"E122"),sQuery(id+"F25.wireOp",EDGE,"E123"),sQuery(id+"F25.wireOp",EDGE,"E124"),sQuery(id+"F25.wireOp",EDGE,"E125"),sQuery(id+"F25.wireOp",EDGE,"E128"),sQuery(id+"F25.wireOp",EDGE,"E129"),subQ2,subQ0,sQuery(id+"F25.wireOp",EDGE,"E132")])],"isStart":true}),makeQuery(id+"F26.opExtrude","SWEPT_FACE",FACE,{"disambiguationData":[OSD([subQ2])]}),makeQuery(id+"F26.opExtrude","SWEPT_FACE",FACE,{"disambiguationData":[OSD([subQ0])]}),makeQuery(id+"F28.opExtrude","SWEPT_FACE",FACE,{"disambiguationData":[OSD([subQ1])]}),subQ3])],"derivedFrom":subQ3});}
            var Q3;
            {var subQ0=sQuery(id+"F27.wireOp",EDGE,"E133");var subQ1=sQuery(id+"F25.wireOp",EDGE,"E130");var subQ2=sQuery(id+"F25.wireOp",EDGE,"E132");var subQ3=sQuery(id+"F25.wireOp",EDGE,"E131");var subQ4=sQuery(id+"F25.wireOp",EDGE,"E129");var subQ5=sQuery(id+"F25.wireOp",EDGE,"E128");var subQ6=sQuery(id+"F25.wireOp",EDGE,"E125");var subQ7=sQuery(id+"F25.wireOp",EDGE,"E124");var subQ8=sQuery(id+"F25.wireOp",EDGE,"E123");var subQ9=sQuery(id+"F25.wireOp",EDGE,"E122");var subQ10=sQuery(id+"F25.wireOp",EDGE,"E121");var subQ11=makeQuery(id+"F28.opExtrude","CAP_FACE",FACE,{"disambiguationData":[OSD([subQ0])],"isStart":true});Q3=makeQuery(id+"F28.boolean.opBoolean","SPLIT",FACE,{"disambiguationData":[TD([makeQuery(id+"F26.opExtrude","CAP_FACE",FACE,{"disambiguationData":[OSD([subQ10,subQ9,subQ8,subQ7,subQ6,subQ5,subQ4,subQ1,subQ3,subQ2])],"isStart":true}),makeQuery(id+"F26.opExtrude","CAP_FACE",FACE,{"disambiguationData":[OSD([subQ10,subQ9,subQ8,subQ7,subQ6,subQ5,subQ4,subQ1,subQ3,subQ2])],"isStart":false}),makeQuery(id+"F26.opExtrude","SWEPT_FACE",FACE,{"disambiguationData":[OSD([subQ1])]}),makeQuery(id+"F28.opExtrude","SWEPT_FACE",FACE,{"disambiguationData":[OSD([subQ0])]}),subQ11])],"derivedFrom":subQ11});}
            extrude(context, id + "F30", {"entities" : qUnion([Q0, Q1, Q2, Q3]), "operationType" : NewBodyOperationType.REMOVE, "oppositeDirection" : true, "depth" : 25.4 * mm, "offsetDistance" : 25.4 * mm});
        }
        {
            var Q0;
            {var subQ0=sQuery(id+"F25.wireOp",EDGE,"E132");Q0=makeQuery(id+"F30.boolean.opBoolean","MERGE",FACE,{"derivedFrom":[makeQuery(id+"F26.opExtrude","CAP_FACE",FACE,{"disambiguationData":[OSD([sQuery(id+"F25.wireOp",EDGE,"E121"),sQuery(id+"F25.wireOp",EDGE,"E122"),sQuery(id+"F25.wireOp",EDGE,"E123"),sQuery(id+"F25.wireOp",EDGE,"E124"),sQuery(id+"F25.wireOp",EDGE,"E125"),sQuery(id+"F25.wireOp",EDGE,"E128"),sQuery(id+"F25.wireOp",EDGE,"E129"),sQuery(id+"F25.wireOp",EDGE,"E130"),sQuery(id+"F25.wireOp",EDGE,"E131"),subQ0])],"isStart":false}),makeQuery(id+"F30.opExtrude","SWEPT_FACE",FACE,{"disambiguationData":[OSD([subQ0]),TDD([makeQuery(id+"F26.opExtrude","CAP_EDGE",EDGE,{"disambiguationData":[OSD([subQ0])],"isStart":false})])]})]});}
            var sketch = newSketch(context, id + "F31", { "sketchPlane" : qUnion([Q0])});
            skLineSegment(sketch, "E134", {"start": v(51.74, 21.72) * mm, "end": v(57.45, 21.72) * mm});
            skLineSegment(sketch, "E135", {"start": v(57.45, 21.72) * mm, "end": v(57.45, 19.36) * mm});
            skLineSegment(sketch, "E136", {"start": v(57.45, 19.36) * mm, "end": v(51.74, 19.36) * mm});
            skLineSegment(sketch, "E137", {"start": v(51.74, 19.36) * mm, "end": v(51.74, 21.72) * mm});
            skLineSegment(sketch, "E138", {"start": v(51.74, 17.6) * mm, "end": v(57.45, 17.6) * mm});
            skLineSegment(sketch, "E139", {"start": v(57.45, 17.6) * mm, "end": v(57.45, 15.24) * mm});
            skLineSegment(sketch, "E140", {"start": v(57.45, 15.24) * mm, "end": v(51.74, 15.24) * mm});
            skLineSegment(sketch, "E141", {"start": v(51.74, 15.24) * mm, "end": v(51.74, 17.6) * mm});
            skSolve(sketch);
        }
        {
            var Q0;
            Q0=makeQuery(id+"F31.imprint","IMPRINT",FACE,{"disambiguationData":[TD([[makeQuery(id+"F31.imprint","IMPRINT",EDGE,{"derivedFrom":sQuery(id+"F31.wireOp",EDGE,"E134")}),-1.0]])]});
            var Q1;
            Q1=makeQuery(id+"F31.imprint","IMPRINT",FACE,{"disambiguationData":[TD([[makeQuery(id+"F31.imprint","IMPRINT",EDGE,{"derivedFrom":sQuery(id+"F31.wireOp",EDGE,"E138")}),-1.0]])]});
            extrude(context, id + "F32", {"entities" : qUnion([Q0, Q1]), "operationType" : NewBodyOperationType.REMOVE, "oppositeDirection" : true, "depth" : 0.76 * mm, "offsetDistance" : 25.4 * mm});
        }
        {
            var Q0;
            Q0=makeQuery(id+"F32.boolean.opBoolean","COPY",FACE,{"derivedFrom":makeQuery(id+"F32.opExtrude","CAP_FACE",FACE,{"disambiguationData":[OSD([sQuery(id+"F31.wireOp",EDGE,"E134"),sQuery(id+"F31.wireOp",EDGE,"E135"),sQuery(id+"F31.wireOp",EDGE,"E136"),sQuery(id+"F31.wireOp",EDGE,"E137")])],"isStart":false})});
            extrude(context, id + "F33", {"entities" : qUnion([Q0]), "depth" : 0.76 * mm, "offsetDistance" : 25.4 * mm});
        }
        {
            var Q0;
            Q0=makeQuery(id+"F32.boolean.opBoolean","COPY",FACE,{"derivedFrom":makeQuery(id+"F32.opExtrude","CAP_FACE",FACE,{"disambiguationData":[OSD([sQuery(id+"F31.wireOp",EDGE,"E138"),sQuery(id+"F31.wireOp",EDGE,"E139"),sQuery(id+"F31.wireOp",EDGE,"E140"),sQuery(id+"F31.wireOp",EDGE,"E141")])],"isStart":false})});
            extrude(context, id + "F34", {"entities" : qUnion([Q0]), "depth" : 0.76 * mm, "offsetDistance" : 25.4 * mm});
        }
    });
